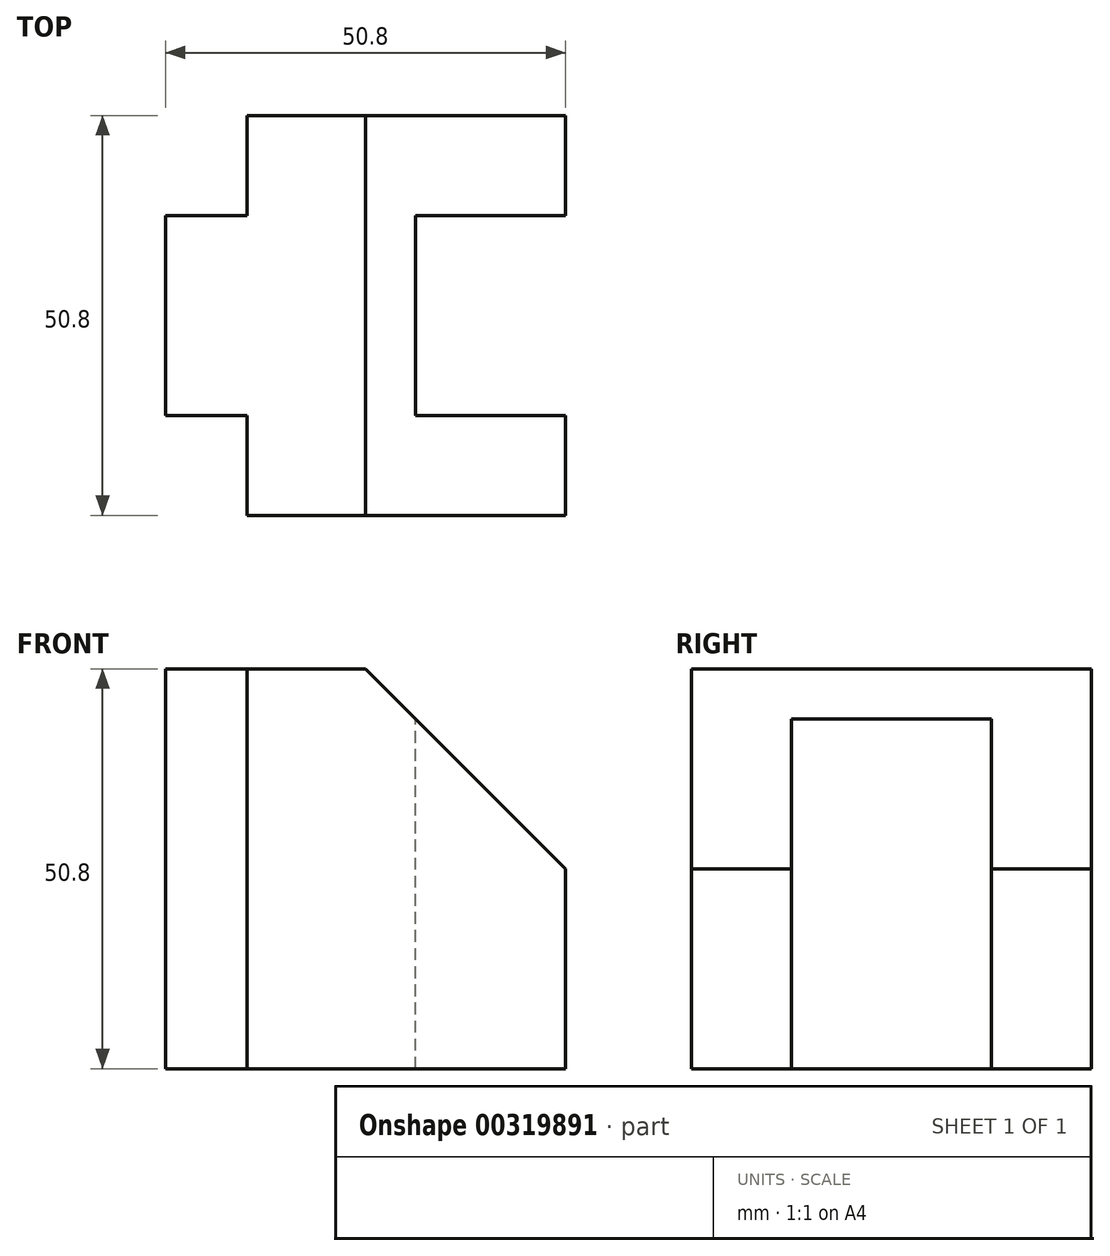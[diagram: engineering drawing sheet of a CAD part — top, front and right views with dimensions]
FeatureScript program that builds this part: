
annotation { "Feature Type Name" : "Feature", "Feature Type Description" : "" }
export const myFeature = defineFeature(function(context is Context, id is Id, definition is map)
    precondition{}
    {
        {
            var Q0;
            Q0=qCreatedBy(makeId("Top.planeOp"),FACE);
            var sketch = newSketch(context, id + "F0", { "sketchPlane" : qUnion([Q0])});
            skLineSegment(sketch, "E0", {"start": v(0, 0) * mm, "end": v(0, 50.8) * mm});
            skLineSegment(sketch, "E1", {"start": v(0, 50.8) * mm, "end": v(50.8, 50.8) * mm});
            skLineSegment(sketch, "E2", {"start": v(50.8, 50.8) * mm, "end": v(50.8, 0) * mm});
            skLineSegment(sketch, "E3", {"start": v(50.8, 0) * mm, "end": v(0, 0) * mm});
            skSolve(sketch);
        }
        {
            var Q0;
            Q0 = qSketchRegion(id + "F0", true);
            extrude(context, id + "F1", {"entities" : qUnion([Q0]), "depth" : 50.8 * mm});
        }
        {
            var Q0;
            Q0=makeQuery(id+"F1.opExtrude","CAP_FACE",FACE,{"disambiguationData":[OSD([sQuery(id+"F0.wireOp",EDGE,"E0"),sQuery(id+"F0.wireOp",EDGE,"E1"),sQuery(id+"F0.wireOp",EDGE,"E2"),sQuery(id+"F0.wireOp",EDGE,"E3")])],"isStart":false});
            var sketch = newSketch(context, id + "F2", { "sketchPlane" : qUnion([Q0])});
            skLineSegment(sketch, "E4", {"start": v(50.8, 38.1) * mm, "end": v(31.75, 38.1) * mm});
            skLineSegment(sketch, "E5", {"start": v(31.75, 38.1) * mm, "end": v(31.75, 12.7) * mm});
            skLineSegment(sketch, "E6", {"start": v(31.75, 12.7) * mm, "end": v(50.8, 12.7) * mm});
            skLineSegment(sketch, "E7", {"start": v(50.8, 12.7) * mm, "end": v(50.8, 38.1) * mm});
            skLineSegment(sketch, "E8", {"start": v(0, 25.4) * mm, "end": v(50.8, 25.4) * mm, "construction": true});
            skSolve(sketch);
        }
        {
            var Q0;
            Q0 = qSketchRegion(id + "F2", true);
            extrude(context, id + "F3", {"entities" : qUnion([Q0]), "operationType" : NewBodyOperationType.REMOVE, "endBound" : BoundingType.THROUGH_ALL, "oppositeDirection" : true, "depth" : 25.4 * mm});
        }
        {
            var Q0;
            Q0=makeQuery(id+"F1.opExtrude","SWEPT_FACE",FACE,{"disambiguationData":[OSD([sQuery(id+"F0.wireOp",EDGE,"E3")])]});
            var sketch = newSketch(context, id + "F4", { "sketchPlane" : qUnion([Q0])});
            skLineSegment(sketch, "E9", {"start": v(50.8, 25.4) * mm, "end": v(25.4, 50.8) * mm});
            skLineSegment(sketch, "E10", {"start": v(25.4, 50.8) * mm, "end": v(50.8, 50.8) * mm});
            skLineSegment(sketch, "E11", {"start": v(50.8, 50.8) * mm, "end": v(50.8, 25.4) * mm});
            skSolve(sketch);
        }
        {
            var Q0;
            Q0 = qSketchRegion(id + "F4", true);
            extrude(context, id + "F5", {"entities" : qUnion([Q0]), "operationType" : NewBodyOperationType.REMOVE, "endBound" : BoundingType.THROUGH_ALL, "oppositeDirection" : true, "depth" : 25.4 * mm});
        }
        {
            var Q0;
            Q0=makeQuery(id+"F1.opExtrude","CAP_FACE",FACE,{"disambiguationData":[OSD([sQuery(id+"F0.wireOp",EDGE,"E0"),sQuery(id+"F0.wireOp",EDGE,"E1"),sQuery(id+"F0.wireOp",EDGE,"E2"),sQuery(id+"F0.wireOp",EDGE,"E3")])],"isStart":false});
            var sketch = newSketch(context, id + "F6", { "sketchPlane" : qUnion([Q0])});
            skLineSegment(sketch, "E12", {"start": v(10.35, 50.8) * mm, "end": v(10.35, 38.1) * mm});
            skLineSegment(sketch, "E13", {"start": v(10.35, 38.1) * mm, "end": v(0, 38.1) * mm});
            skLineSegment(sketch, "E14", {"start": v(0, 38.1) * mm, "end": v(0, 12.7) * mm});
            skLineSegment(sketch, "E15", {"start": v(0, 12.7) * mm, "end": v(10.35, 12.7) * mm});
            skLineSegment(sketch, "E16", {"start": v(10.35, 12.7) * mm, "end": v(10.35, 0) * mm});
            skLineSegment(sketch, "E17", {"start": v(10.35, 0) * mm, "end": v(0, 0) * mm});
            skLineSegment(sketch, "E18", {"start": v(0, 0) * mm, "end": v(0, 50.8) * mm});
            skLineSegment(sketch, "E19", {"start": v(0, 50.8) * mm, "end": v(10.35, 50.8) * mm});
            skSolve(sketch);
        }
        {
            var Q0;
            Q0 = qSketchRegion(id + "F6", true);
            extrude(context, id + "F7", {"entities" : qUnion([Q0]), "operationType" : NewBodyOperationType.REMOVE, "endBound" : BoundingType.THROUGH_ALL, "oppositeDirection" : true, "depth" : 25.4 * mm});
        }
    });
